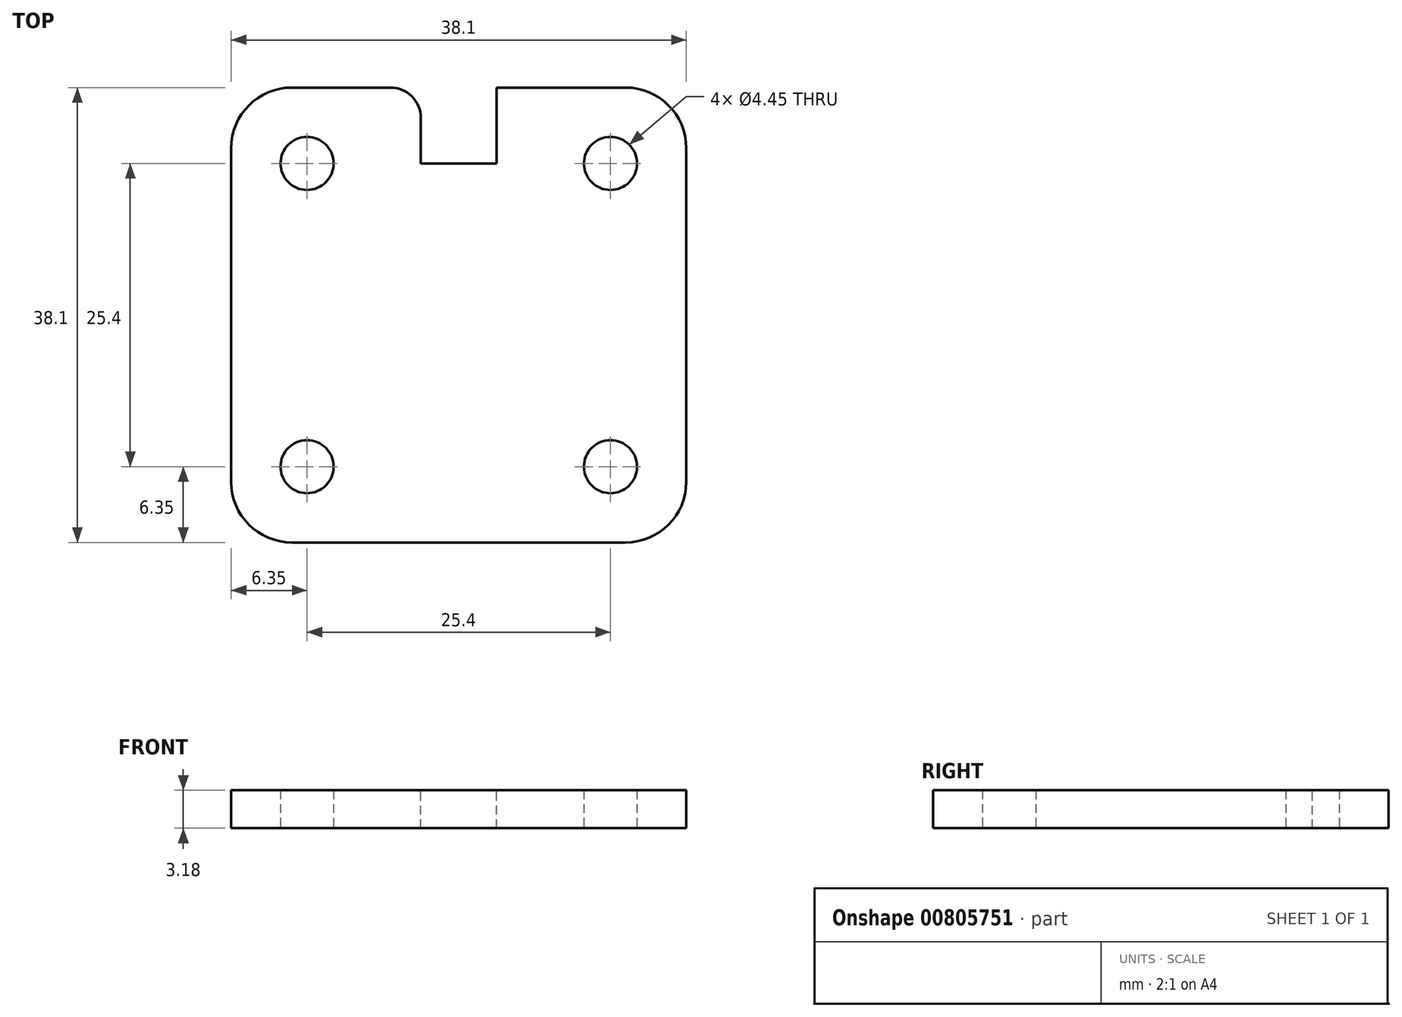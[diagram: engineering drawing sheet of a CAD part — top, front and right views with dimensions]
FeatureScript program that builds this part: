
annotation { "Feature Type Name" : "Feature", "Feature Type Description" : "" }
export const myFeature = defineFeature(function(context is Context, id is Id, definition is map)
    precondition{}
    {
        {
            var Q0;
            Q0=qCreatedBy(makeId("Top.planeOp"),FACE);
            var sketch = newSketch(context, id + "F0", { "sketchPlane" : qUnion([Q0])});
            skLineSegment(sketch, "E0.bottom", {"start": v(19.05, 19.05) * mm, "end": v(-19.05, 19.05) * mm});
            skLineSegment(sketch, "E0.top", {"start": v(19.05, -19.05) * mm, "end": v(-19.05, -19.05) * mm});
            skLineSegment(sketch, "E0.left", {"start": v(19.05, 19.05) * mm, "end": v(19.05, -19.05) * mm});
            skLineSegment(sketch, "E0.right", {"start": v(-19.05, 19.05) * mm, "end": v(-19.05, -19.05) * mm});
            skPoint(sketch, "E0.middle", {"position": v(0, 0) * mm});
            skCircle(sketch, "E1", {"center": v(-12.7, 12.7) * mm, "radius": 2.22 * mm});
            skCircle(sketch, "E2", {"center": v(-12.7, -12.7) * mm, "radius": 2.22 * mm});
            skCircle(sketch, "E3", {"center": v(12.7, 12.7) * mm, "radius": 2.22 * mm});
            skCircle(sketch, "E4", {"center": v(12.7, -12.7) * mm, "radius": 2.22 * mm});
            skSolve(sketch);
        }
        {
            var Q0;
            Q0 = qSketchRegion(id + "F0", true);
            extrude(context, id + "F1", {"entities" : qUnion([Q0]), "depth" : 3.17 * mm, "offsetDistance" : 25.4 * mm});
        }
        {
            var Q0;
            Q0=makeQuery(id+"F1.opExtrude","SWEPT_EDGE",EDGE,{"disambiguationData":[OSD([sQuery(id+"F0.wireOp",EDGE,"E0.top"),sQuery(id+"F0.wireOp",EDGE,"E0.left")])]});
            var Q1;
            Q1=makeQuery(id+"F1.opExtrude","SWEPT_EDGE",EDGE,{"disambiguationData":[OSD([sQuery(id+"F0.wireOp",EDGE,"E0.bottom"),sQuery(id+"F0.wireOp",EDGE,"E0.left")])]});
            var Q2;
            Q2=makeQuery(id+"F1.opExtrude","SWEPT_EDGE",EDGE,{"disambiguationData":[OSD([sQuery(id+"F0.wireOp",EDGE,"E0.top"),sQuery(id+"F0.wireOp",EDGE,"E0.right")])]});
            var Q3;
            Q3=makeQuery(id+"F1.opExtrude","SWEPT_EDGE",EDGE,{"disambiguationData":[OSD([sQuery(id+"F0.wireOp",EDGE,"E0.bottom"),sQuery(id+"F0.wireOp",EDGE,"E0.right")])]});
            fillet(context, id + "F2", {"entities" : qUnion([Q0, Q1, Q2, Q3]), "radius" : 5.08 * mm, "tangentPropagation" : true, "allowEdgeOverflow" : false});
        }
        {
            var Q0;
            Q0=makeQuery(id+"F1.opExtrude","CAP_FACE",FACE,{"disambiguationData":[OSD([sQuery(id+"F0.wireOp",EDGE,"E0.bottom"),sQuery(id+"F0.wireOp",EDGE,"E0.top"),sQuery(id+"F0.wireOp",EDGE,"E0.left"),sQuery(id+"F0.wireOp",EDGE,"E0.right"),sQuery(id+"F0.wireOp",EDGE,"E1"),sQuery(id+"F0.wireOp",EDGE,"E2"),sQuery(id+"F0.wireOp",EDGE,"E3"),sQuery(id+"F0.wireOp",EDGE,"E4")])],"isStart":false});
            var sketch = newSketch(context, id + "F3", { "sketchPlane" : qUnion([Q0])});
            skLineSegment(sketch, "E5.bottom", {"start": v(3.17, 19.05) * mm, "end": v(-3.18, 19.05) * mm});
            skLineSegment(sketch, "E5.top", {"start": v(3.18, 12.7) * mm, "end": v(-3.17, 12.7) * mm});
            skLineSegment(sketch, "E5.left", {"start": v(3.17, 19.05) * mm, "end": v(3.18, 12.7) * mm});
            skLineSegment(sketch, "E5.right", {"start": v(-3.18, 19.05) * mm, "end": v(-3.17, 12.7) * mm});
            skSolve(sketch);
        }
        {
            var Q0;
            Q0 = qSketchRegion(id + "F3", true);
            extrude(context, id + "F4", {"entities" : qUnion([Q0]), "operationType" : NewBodyOperationType.REMOVE, "oppositeDirection" : true, "depth" : 25.4 * mm, "offsetDistance" : 25.4 * mm});
        }
        {
            var Q0;
            Q0=makeQuery(id+"F4.boolean.opBoolean","COPY",EDGE,{"derivedFrom":makeQuery(id+"F4.opExtrude","SWEPT_EDGE",EDGE,{"disambiguationData":[OSD([sQuery(id+"F0.wireOp",EDGE,"E0.bottom"),sQuery(id+"F3.wireOp",EDGE,"E5.bottom"),sQuery(id+"F3.wireOp",EDGE,"E5.right")])]})});
            var Q1;
            Q1=makeQuery(id+"F4.boolean.opBoolean","COPY",EDGE,{"derivedFrom":makeQuery(id+"F4.opExtrude","SWEPT_EDGE",EDGE,{"disambiguationData":[OSD([sQuery(id+"F0.wireOp",EDGE,"E0.bottom"),sQuery(id+"F3.wireOp",EDGE,"E5.bottom"),sQuery(id+"F3.wireOp",EDGE,"E5.left")])]})});
            fillet(context, id + "F5", {"entities" : qUnion([Q0, Q1]), "radius" : 2.54 * mm, "tangentPropagation" : true, "allowEdgeOverflow" : false});
        }
    });
